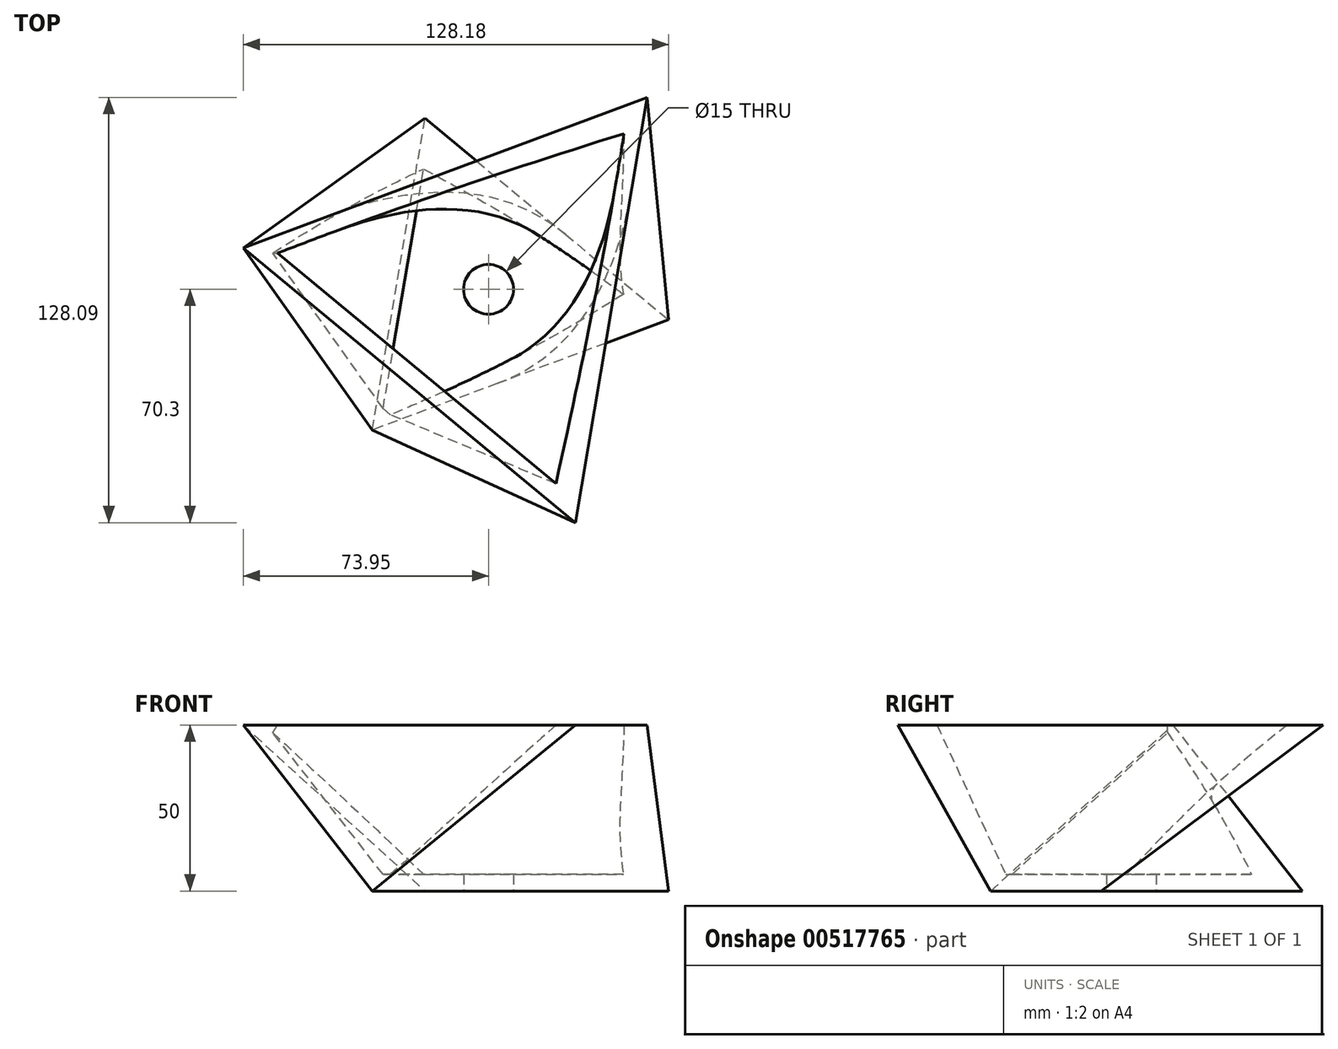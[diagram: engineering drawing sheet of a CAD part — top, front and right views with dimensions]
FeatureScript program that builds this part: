
annotation { "Feature Type Name" : "Feature", "Feature Type Description" : "" }
export const myFeature = defineFeature(function(context is Context, id is Id, definition is map)
    precondition{}
    {
        {
            var Q0;
            Q0=qCreatedBy(makeId("Top.planeOp"),FACE);
            var sketch = newSketch(context, id + "F0", { "sketchPlane" : qUnion([Q0])});
            skCircle(sketch, "E0.cCircle", {"center": v(0, 0) * mm, "radius": 27.5 * mm, "construction": true});
            skLineSegment(sketch, "E0.0", {"start": v(-19.17, 51.55) * mm, "end": v(54.23, -9.17) * mm});
            skLineSegment(sketch, "E0.1", {"start": v(54.23, -9.17) * mm, "end": v(-35.06, -42.38) * mm});
            skLineSegment(sketch, "E0.2", {"start": v(-35.06, -42.38) * mm, "end": v(-19.17, 51.55) * mm});
            skPoint(sketch, "E0.0.midPoint", {"position": v(17.53, 21.19) * mm});
            skSolve(sketch);
        }
        {
            var Q0;
            Q0=qCreatedBy(makeId("Top.planeOp"),FACE);
            cPlane(context, id + "F1", {"entities" : qUnion([Q0]), "cplaneType" : CPlaneType.OFFSET, "offset" : 50 * mm, "width" : 150 * mm, "height" : 150 * mm});
        }
        {
            var Q0;
            Q0=qCreatedBy(id+"F1.planeOp",FACE);
            var sketch = newSketch(context, id + "F2", { "sketchPlane" : qUnion([Q0])});
            skCircle(sketch, "E1.cCircle", {"center": v(0, 0) * mm, "radius": 37.5 * mm, "construction": true});
            skLineSegment(sketch, "E1.0", {"start": v(47.8, 57.79) * mm, "end": v(26.14, -70.3) * mm});
            skLineSegment(sketch, "E1.1", {"start": v(26.14, -70.3) * mm, "end": v(-73.95, 12.5) * mm});
            skLineSegment(sketch, "E1.2", {"start": v(-73.95, 12.5) * mm, "end": v(47.8, 57.79) * mm});
            skPoint(sketch, "E1.0.midPoint", {"position": v(36.97, -6.25) * mm});
            skLineSegment(sketch, "E2", {"start": v(47.8, 57.79) * mm, "end": v(-23.9, -28.9) * mm, "construction": true});
            skPoint(sketch, "E3.0", {"position": v(17.53, 21.19) * mm});
            skSolve(sketch);
        }
        {
            var Q0;
            Q0=sQuery(id+"F2.wireOp",VERTEX,"E1.2.start");
            var Q1;
            Q1=sQuery(id+"F2.wireOp",VERTEX,"E1.1.start");
            var Q2;
            Q2=sQuery(id+"F0.wireOp",VERTEX,"E0.1.end");
            cPlane(context, id + "F3", {"entities" : qUnion([Q0, Q1, Q2]), "cplaneType" : CPlaneType.THREE_POINT, "offset" : 25 * mm, "width" : 150 * mm, "height" : 150 * mm});
        }
        {
            var Q0;
            Q0=qCreatedBy(id+"F3.planeOp",FACE);
            var sketch = newSketch(context, id + "F4", { "sketchPlane" : qUnion([Q0])});
            skPoint(sketch, "E4.0", {"position": v(-53.48, 50.7) * mm});
            skPoint(sketch, "E5.0", {"position": v(71.83, 16.45) * mm});
            skPoint(sketch, "E6.0", {"position": v(-4.8, -17.53) * mm});
            skLineSegment(sketch, "E7", {"start": v(-53.48, 50.7) * mm, "end": v(71.83, 16.45) * mm});
            skLineSegment(sketch, "E8", {"start": v(71.83, 16.45) * mm, "end": v(-4.8, -17.53) * mm});
            skLineSegment(sketch, "E9", {"start": v(-4.8, -17.53) * mm, "end": v(-53.48, 50.7) * mm});
            skSolve(sketch);
        }
        {
            var Q0;
            Q0=sQuery(id+"F4.wireOp",VERTEX,"E6.0");
            var Q1;
            Q1=sQuery(id+"F4.wireOp",VERTEX,"E4.0");
            var Q2;
            Q2=sQuery(id+"F0.wireOp",VERTEX,"E0.0.start");
            cPlane(context, id + "F5", {"entities" : qUnion([Q0, Q1, Q2]), "cplaneType" : CPlaneType.THREE_POINT, "offset" : 25 * mm, "width" : 150 * mm, "height" : 150 * mm});
        }
        {
            var Q0;
            Q0=qCreatedBy(id+"F5.planeOp",FACE);
            var sketch = newSketch(context, id + "F6", { "sketchPlane" : qUnion([Q0])});
            skPoint(sketch, "E10.0", {"position": v(10.17, 87.32) * mm});
            skPoint(sketch, "E11.0", {"position": v(-45.12, 24.33) * mm});
            skPoint(sketch, "E12.0", {"position": v(49.5, 13.3) * mm});
            skLineSegment(sketch, "E13", {"start": v(10.17, 87.32) * mm, "end": v(49.5, 13.3) * mm});
            skLineSegment(sketch, "E14", {"start": v(49.5, 13.3) * mm, "end": v(-45.12, 24.33) * mm});
            skLineSegment(sketch, "E15", {"start": v(-45.12, 24.33) * mm, "end": v(10.17, 87.32) * mm});
            skSolve(sketch);
        }
        {
            var Q0;
            Q0=makeQuery(id+"F2.imprint","IMPRINT",FACE,{"disambiguationData":[TD([[makeQuery(id+"F2.imprint","IMPRINT",EDGE,{"derivedFrom":sQuery(id+"F2.wireOp",EDGE,"E1.0")}),-1.0]])]});
            var Q1;
            Q1=makeQuery(id+"F0.imprint","IMPRINT",FACE,{"disambiguationData":[TD([[makeQuery(id+"F0.imprint","IMPRINT",EDGE,{"derivedFrom":sQuery(id+"F0.wireOp",EDGE,"E0.0")}),-1.0]])]});
            loft(context, id + "F7", {"sheetProfilesArray" : [{ "sheetProfileEntities" : qUnion([Q0]) }, { "sheetProfileEntities" : qUnion([Q1]) }]});
        }
        {
            var Q0;
            Q0 = qSketchRegion(id + "F4", true);
            var Q1;
            Q1 = qSketchRegion(id + "F6", true);
            var Q2;
            Q2=makeQuery(id+"F7.opLoft","SWEPT_BODY",BODY,{"disambiguationData":[OSD([makeQuery(id+"F0.imprint","IMPRINT",FACE,{"disambiguationData":[TD([[makeQuery(id+"F0.imprint","IMPRINT",EDGE,{"derivedFrom":sQuery(id+"F0.wireOp",EDGE,"E0.0")}),-1.0]])]}),makeQuery(id+"F2.imprint","IMPRINT",FACE,{"disambiguationData":[TD([[makeQuery(id+"F2.imprint","IMPRINT",EDGE,{"derivedFrom":sQuery(id+"F2.wireOp",EDGE,"E1.0")}),-1.0]])]})])]});
            extrude(context, id + "F8", {"entities" : qUnion([Q0, Q1]), "operationType" : NewBodyOperationType.ADD, "endBound" : BoundingType.UP_TO_BODY, "oppositeDirection" : true, "depth" : 25 * mm, "endBoundEntityBody" : qUnion([Q2]), "offsetDistance" : 25 * mm});
        }
        {
            var Q0;
            Q0=makeQuery(id+"F7.opLoft","CAP_FACE",FACE,{"disambiguationData":[OSD([makeQuery(id+"F2.imprint","IMPRINT",FACE,{"disambiguationData":[TD([[makeQuery(id+"F2.imprint","IMPRINT",EDGE,{"derivedFrom":sQuery(id+"F2.wireOp",EDGE,"E1.0")}),-1.0]])]})])],"isStart":true});
            shell(context, id + "F9", {"entities" : qUnion([Q0]), "thickness" : 5 * mm});
        }
        {
            var Q0;
            Q0=sQuery(id+"F0.wireOp",VERTEX,"E0.cCircle.center");
            var Q1;
            Q1=makeQuery(id+"F7.opLoft","SWEPT_BODY",BODY,{"disambiguationData":[OSD([makeQuery(id+"F0.imprint","IMPRINT",FACE,{"disambiguationData":[TD([[makeQuery(id+"F0.imprint","IMPRINT",EDGE,{"derivedFrom":sQuery(id+"F0.wireOp",EDGE,"E0.0")}),-1.0]])]}),makeQuery(id+"F2.imprint","IMPRINT",FACE,{"disambiguationData":[TD([[makeQuery(id+"F2.imprint","IMPRINT",EDGE,{"derivedFrom":sQuery(id+"F2.wireOp",EDGE,"E1.0")}),-1.0]])]})])]});
            hole(context, id + "F10", {"style" : HoleStyle.SIMPLE, "endStyle" : HoleEndStyle.THROUGH, "oppositeDirection" : true, "holeDiameter" : 15 * mm, "isTappedThrough" : true, "tappedDepth" : 12 * mm, "tapClearance" : 3, "startFromSketch" : true, "locations" : qUnion([Q0]), "scope" : qUnion([Q1])});
        }
    });
